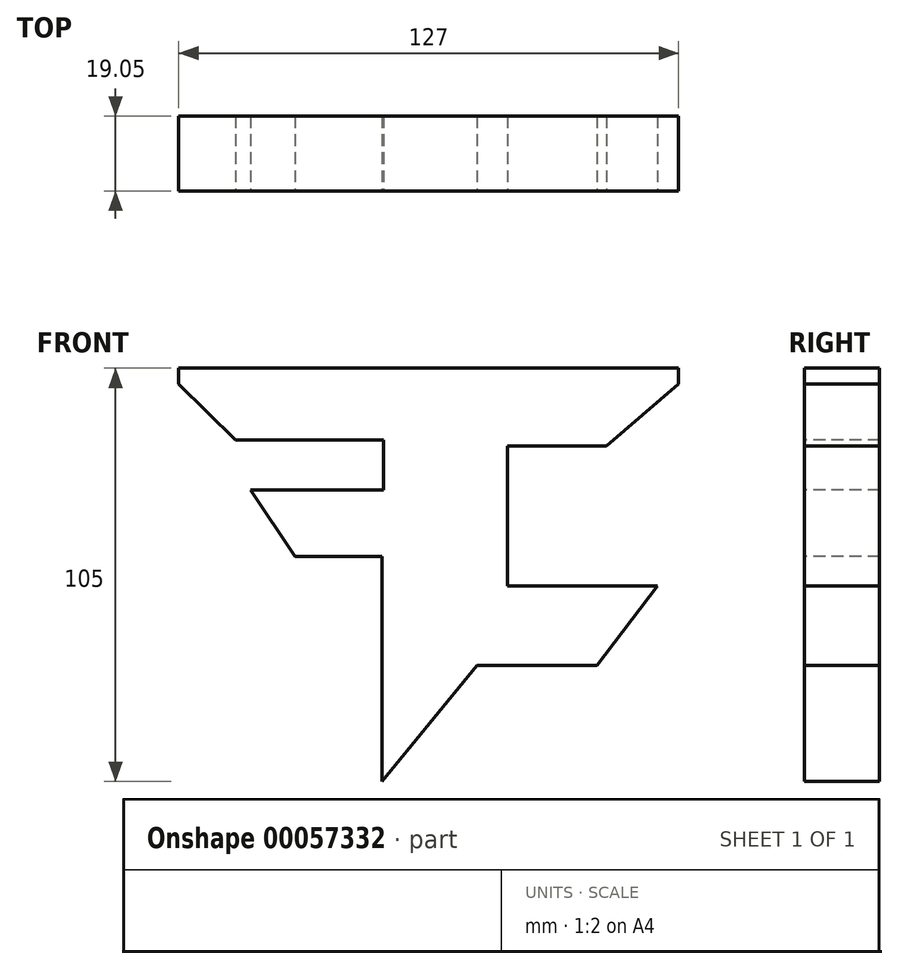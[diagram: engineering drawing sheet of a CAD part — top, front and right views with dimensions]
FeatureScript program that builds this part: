
annotation { "Feature Type Name" : "Feature", "Feature Type Description" : "" }
export const myFeature = defineFeature(function(context is Context, id is Id, definition is map)
    precondition{}
    {
        {
            var Q0;
            Q0=qCreatedBy(makeId("Front.planeOp"),FACE);
            var sketch = newSketch(context, id + "F0", { "sketchPlane" : qUnion([Q0])});
            skLineSegment(sketch, "E0", {"start": v(-71.29, 62.28) * mm, "end": v(55.71, 62.28) * mm});
            skLineSegment(sketch, "E1", {"start": v(55.71, 62.28) * mm, "end": v(55.71, -64.72) * mm});
            skLineSegment(sketch, "E2", {"start": v(55.71, -64.72) * mm, "end": v(-71.29, -64.72) * mm});
            skLineSegment(sketch, "E3", {"start": v(-71.29, -64.72) * mm, "end": v(-71.29, 62.28) * mm});
            skSolve(sketch);
        }
        {
            var Q0;
            Q0=makeQuery(id+"F0.imprint","IMPRINT",FACE,{"disambiguationData":[TD([[makeQuery(id+"F0.imprint","IMPRINT",EDGE,{"derivedFrom":sQuery(id+"F0.wireOp",EDGE,"E0")}),-1.0]])]});
            extrude(context, id + "F1", {"entities" : qUnion([Q0]), "depth" : 19.05 * mm});
        }
        {
            var Q0;
            Q0=makeQuery(id+"F1.opExtrude","CAP_FACE",FACE,{"disambiguationData":[OSD([sQuery(id+"F0.wireOp",EDGE,"E0"),sQuery(id+"F0.wireOp",EDGE,"E1"),sQuery(id+"F0.wireOp",EDGE,"E2"),sQuery(id+"F0.wireOp",EDGE,"E3")])],"isStart":false});
            var sketch = newSketch(context, id + "F2", { "sketchPlane" : qUnion([Q0])});
            skLineSegment(sketch, "E4", {"start": v(-71.29, 58.3) * mm, "end": v(55.71, 58.3) * mm});
            skLineSegment(sketch, "E5", {"start": v(-71.29, 58.3) * mm, "end": v(-56.83, 44.02) * mm});
            skLineSegment(sketch, "E6", {"start": v(37.45, 42.53) * mm, "end": v(55.71, 58.3) * mm});
            skLineSegment(sketch, "E7", {"start": v(-56.83, 44.02) * mm, "end": v(-19.23, 44.02) * mm});
            skLineSegment(sketch, "E8", {"start": v(37.45, 42.53) * mm, "end": v(12.24, 42.53) * mm});
            skLineSegment(sketch, "E9", {"start": v(-19.23, 44.02) * mm, "end": v(-19.23, 31.32) * mm});
            skLineSegment(sketch, "E10", {"start": v(-19.23, 31.32) * mm, "end": v(-53.06, 31.32) * mm});
            skLineSegment(sketch, "E11", {"start": v(-53.06, 31.32) * mm, "end": v(-41.74, 14.45) * mm});
            skLineSegment(sketch, "E12", {"start": v(-41.74, 14.45) * mm, "end": v(-19.65, 14.45) * mm});
            skLineSegment(sketch, "E13", {"start": v(12.24, 42.53) * mm, "end": v(12.24, 6.97) * mm});
            skLineSegment(sketch, "E14", {"start": v(12.24, 6.97) * mm, "end": v(50.34, 6.97) * mm});
            skLineSegment(sketch, "E15", {"start": v(50.34, 6.97) * mm, "end": v(35.03, -13.3) * mm});
            skLineSegment(sketch, "E16", {"start": v(35.03, -13.3) * mm, "end": v(4.55, -13.3) * mm});
            skLineSegment(sketch, "E17", {"start": v(-19.65, 14.45) * mm, "end": v(-19.65, -42.72) * mm});
            skLineSegment(sketch, "E18", {"start": v(-19.65, -42.72) * mm, "end": v(4.55, -13.3) * mm});
            skSolve(sketch);
        }
        {
            var Q0;
            {var subQ0=sQuery(id+"F2.wireOp",EDGE,"E5");Q0=makeQuery(id+"F2.imprint","IMPRINT",FACE,{"disambiguationData":[TD([[makeQuery(id+"F2.imprint","IMPRINT",EDGE,{"derivedFrom":subQ0}),-1.0]])]});}
            extrude(context, id + "F3", {"entities" : qUnion([Q0]), "operationType" : NewBodyOperationType.REMOVE, "oppositeDirection" : true, "depth" : 25.4 * mm});
        }
    });
